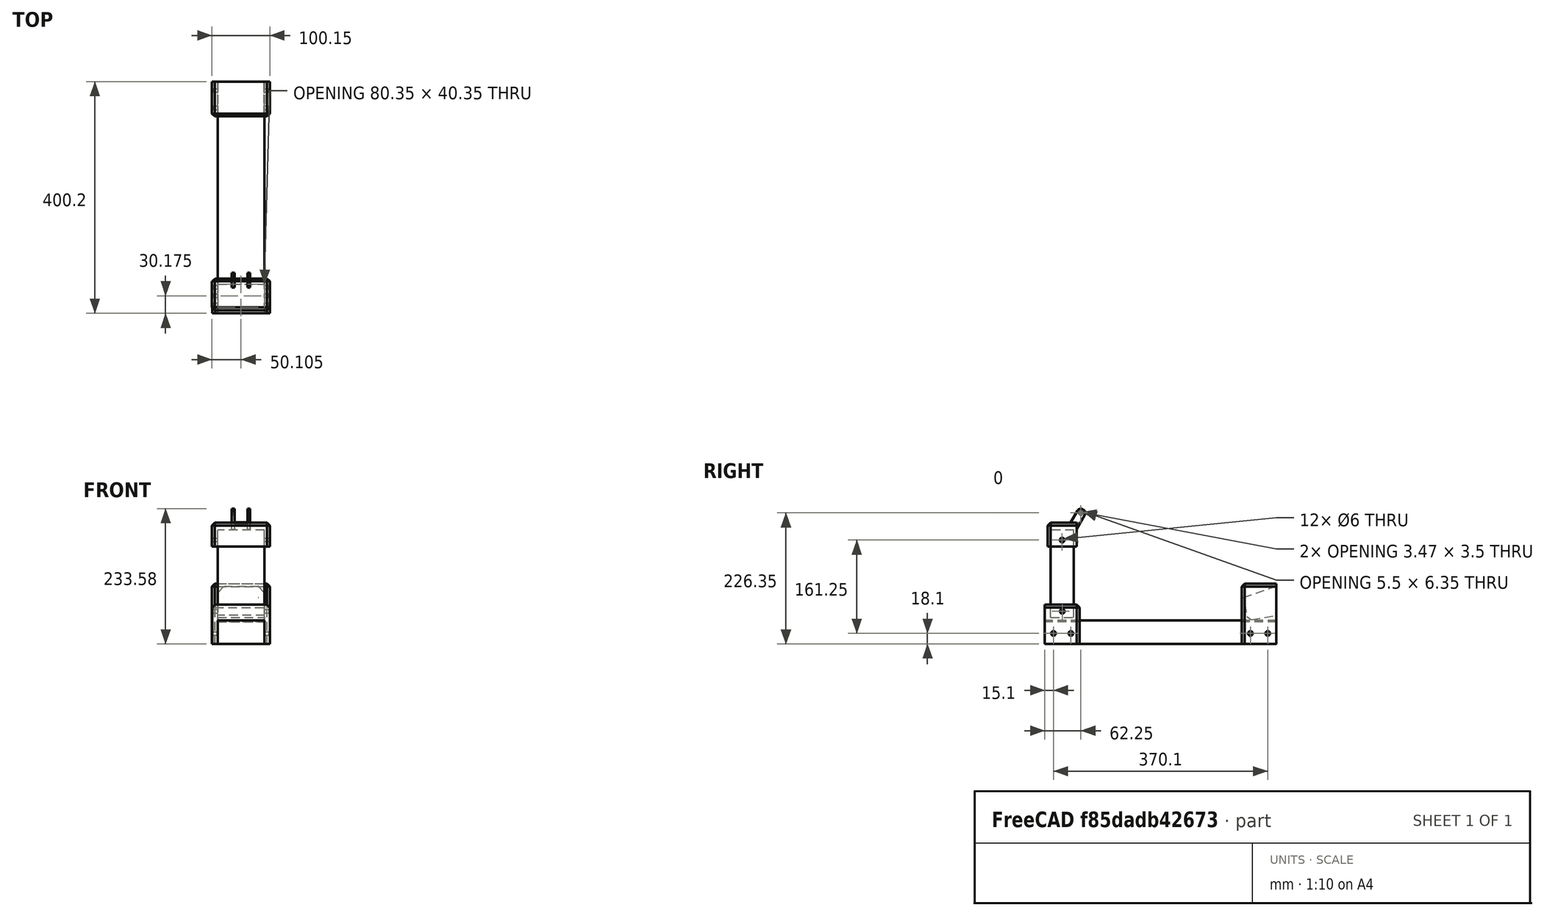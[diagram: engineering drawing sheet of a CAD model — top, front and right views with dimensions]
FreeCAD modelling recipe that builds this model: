
FCSTD DOCUMENT  (FreeCAD 0.19R24276 (Git))
Label: Coil4VapingMaker
License: All rights reserved
LicenseURL: http://en.wikipedia.org/wiki/All_rights_reserved
objects: TechDraw::DrawViewDimension×57, TechDraw::DrawProjGroupItem×9, TechDraw::DrawSVGTemplate×8, TechDraw::DrawViewPart×8, TechDraw::DrawPage×8, Part::Chamfer×6, Part::Box×5, Part::Offset×5, Part::Cut×5, Part::Cylinder×5, Part::Feature×3, TechDraw::DrawProjGroup×3, TechDraw::DrawViewSection×2, Part::MultiFuse×1
note: 30 computed .brp shape members not serialized (recipe doc carries the construction recipe); baked Part::Feature solids carry a one-line shape summary decoded from their .brp

FEATURE [Part::Feature] Part__Feature  label="Chamfer"
  Placement = pos=(-24.075,55,-200.25) rot=(0,0,1;0rad)
  shape: bbox 100 x 60 x 68 mm, 20 faces (baked)
FEATURE [Part::Box] Box001  label="Cube001"
  AttacherType = Attacher::AttachEngine3D
  Height = 151.15
  Length = 80.15
  Width = 40.15
FEATURE [Part::Offset] Offset  label="Offset001"
  Fill = false
  Intersection = false
  Join = 0
  Mode = 0
  Placement = pos=(-24.1,5,-152.9) rot=(0,0,1;0rad)
  SelfIntersection = false
  Source = -> Box001
  Value = 0.1
FEATURE [Part::Cut] Cut
  Base = -> Part__Feature
  Tool = -> Offset
FEATURE [Part::Chamfer] Chamfer  label="Chamfer001"
  Base = -> Cut
  Edges = 5 edges r=5: [Edge3,Edge4,Edge12,Edge19,Edge20]
FEATURE [Part::Cylinder] Cylinder002
  Angle = 360
  AttacherType = Attacher::AttachEngine3D
  Height = 100
  Placement = pos=(-34,25.25,-142) rot=(0,1,0;1.5708rad)
  Radius = 3
FEATURE [Part::Cut] Cut001
  Base = -> Chamfer
  Tool = -> Cylinder002
FEATURE [Part::Chamfer] Chamfer002  label="BaseHolder"
  Base = -> Cut001
  Edges = 2 edges r=1: [Edge5,Edge64]
FEATURE [Part::Box] Box003  label="Cube003"
  AttacherType = Attacher::AttachEngine3D
  Height = 200
  Length = 80.15
  Placement = pos=(0,0,0) rot=(1,0,0;1.5708rad)
  Width = 40.15
FEATURE [Part::Box] Box004  label="Cube004"
  AttacherType = Attacher::AttachEngine3D
  Height = 60
  Length = 100
  Placement = pos=(-9.925,0,2) rot=(1,0,0;1.5708rad)
  Width = 104
FEATURE [Part::Cylinder] Cylinder004
  Angle = 360
  AttacherType = Attacher::AttachEngine3D
  Height = 11
  Placement = pos=(80,-15,20) rot=(0,1,0;1.5708rad)
  Radius = 3
FEATURE [Part::Cylinder] Cylinder005
  Angle = 360
  AttacherType = Attacher::AttachEngine3D
  Height = 11
  Placement = pos=(80,-45,20) rot=(0,1,0;1.5708rad)
  Radius = 3
FEATURE [Part::Cylinder] Cylinder011
  Angle = 360
  AttacherType = Attacher::AttachEngine3D
  Height = 11
  Placement = pos=(-11,-45,20) rot=(0,1,0;1.5708rad)
  Radius = 3
FEATURE [Part::Cylinder] Cylinder012
  Angle = 360
  AttacherType = Attacher::AttachEngine3D
  Height = 11
  Placement = pos=(-11,-15,20) rot=(0,1,0;1.5708rad)
  Radius = 3
FEATURE [Part::Offset] Offset002  label="Offset003"
  Fill = false
  Intersection = false
  Join = 0
  Mode = 0
  SelfIntersection = false
  Source = -> Box003
  Value = 0.1
FEATURE [Part::MultiFuse] Fusion011
  Shapes = -> [Cylinder004,Cylinder005,Cylinder011,Cylinder012]
FEATURE [Part::Feature] Part__Feature002  label="Pad"
  Placement = pos=(0,0,0) rot=(0.57735,0.57735,0.57735;2.0944rad)
  shape: bbox 80.75 x 65 x 50 mm, 6 faces (baked)
FEATURE [Part::Chamfer] Chamfer001  label="Chamfer006"
  Base = -> Part__Feature002
  Edges = 2 edges r=10.65: [Edge11,Edge12]
FEATURE [Part::Chamfer] Chamfer005  label="Chamfer002"
  Base = -> Chamfer001
  Edges = 1 edges r=6.4: [Edge4]
  Placement = pos=(0,-21,68) rot=(1,0,0;0.174533rad)
FEATURE [Part::Offset] Offset003  label="Offset004"
  Fill = false
  Intersection = false
  Join = 0
  Mode = 0
  SelfIntersection = false
  Source = -> Chamfer005
  Value = 0.1
FEATURE [Part::Cut] Cut004
  Base = -> Box004
  Tool = -> Offset002
FEATURE [Part::Cut] Cut005
  Base = -> Cut004
  Tool = -> Fusion011
FEATURE [Part::Cut] Cut006
  Base = -> Cut005
  Tool = -> Offset003
FEATURE [Part::Chamfer] Chamfer006  label="Chamfer007"
  Base = -> Cut006
  Edges = 4 edges r=1: [Edge5,Edge6,Edge45,Edge46]
FEATURE [Part::Chamfer] Chamfer007  label="DrillHolder"
  Base = -> Chamfer006
  Edges = 5 edges r=5: [Edge4,Edge5,Edge12,Edge13,Edge40]
  Placement = pos=(-24.175,395.1,-200.25) rot=(0,0,1;0rad)
FEATURE [Part::Box] Box005  label="Cube005"
  AttacherType = Attacher::AttachEngine3D
  Height = 151.15
  Length = 80.15
  Width = 40.15
FEATURE [Part::Offset] Offset004  label="AluminumProfile_Vert"
  Fill = false
  Intersection = false
  Join = 0
  Mode = 0
  Placement = pos=(-24.1,5,-152.9) rot=(0,0,1;0rad)
  SelfIntersection = false
  Source = -> Box005
  Value = 0.1
FEATURE [Part::Box] Box006  label="Cube006"
  AttacherType = Attacher::AttachEngine3D
  Height = 400
  Length = 80.15
  Placement = pos=(0,0,0) rot=(1,0,0;1.5708rad)
  Width = 40.15
FEATURE [Part::Offset] Offset005  label="AluminumProfile_Hor"
  Fill = false
  Intersection = false
  Join = 0
  Mode = 0
  Placement = pos=(-24.075,395,-198.25) rot=(0,0,1;0rad)
  SelfIntersection = false
  Source = -> Box006
  Value = 0.1
FEATURE [Part::Feature] Part__Feature003  label="ClaptonJig"
  Placement = pos=(31.95,50.15,-6e-15) rot=(0,0,1;3.14159rad)
  shape: bbox 100.2 x 64.92 x 65.08 mm, 286 faces (baked)
FEATURE [TechDraw::DrawSVGTemplate] Template
  EditableTexts = Designed_by_Name=<owner>; Drawing_number=001; FC-Date=12/08/21; FC-SC=1:2; FC-SH=1/8; FC-Title=DrillHolder; Subtitle=Soporte Taladro; Weight=<250gr
  Height = 210
  Orientation = 1
  Width = 297
FEATURE [TechDraw::DrawViewPart] View
  CoarseView = false
  Direction = (0.577,-0.577,0.577)
  Focus = 100
  HardHidden = false
  IsoCount = 0
  IsoHidden = false
  IsoVisible = false
  LockPosition = false
  Perspective = false
  Rotation = 0
  Scale = 0.5
  ScaleType = 0
  SeamHidden = false
  SeamVisible = true
  SmoothHidden = false
  SmoothVisible = true
  Source = -> [Chamfer007]
  X = 213.955
  XDirection = (0.707,0.707,0)
  Y = 142.792
FEATURE [TechDraw::DrawProjGroupItem] ProjItem  label="Front"
  CoarseView = false
  Direction = (0,-1,0)
  Focus = 100
  HardHidden = false
  IsoCount = 0
  IsoHidden = false
  IsoVisible = false
  LockPosition = true
  Perspective = false
  Rotation = 0
  RotationVector = (1,0,0)
  ScaleType = 2
  SeamHidden = false
  SeamVisible = true
  SmoothHidden = false
  SmoothVisible = true
  Source = -> [Chamfer007]
  Type = 0
  X = 0
  XDirection = (1,0,0)
  Y = 0
FEATURE [TechDraw::DrawProjGroupItem] ProjItem001  label="Right"
  CoarseView = false
  Direction = (1,-1e-16,0)
  Focus = 100
  HardHidden = false
  IsoCount = 0
  IsoHidden = false
  IsoVisible = false
  LockPosition = false
  Perspective = false
  Rotation = 0
  RotationVector = (1,0,0)
  ScaleType = 2
  SeamHidden = false
  SeamVisible = true
  SmoothHidden = false
  SmoothVisible = true
  Source = -> [Chamfer007]
  Type = 2
  X = -54.9943
  XDirection = (1e-16,1,0)
  Y = 0
FEATURE [TechDraw::DrawProjGroupItem] ProjItem002  label="Top"
  CoarseView = false
  Direction = (0,0,1)
  Focus = 100
  HardHidden = false
  IsoCount = 0
  IsoHidden = false
  IsoVisible = false
  LockPosition = false
  Perspective = false
  Rotation = 0
  RotationVector = (1,0,0)
  ScaleType = 2
  SeamHidden = false
  SeamVisible = true
  SmoothHidden = false
  SmoothVisible = true
  Source = -> [Chamfer007]
  Type = 4
  X = 0
  XDirection = (1,0,0)
  Y = -77.9943
FEATURE [TechDraw::DrawProjGroup] ProjGroup
  Anchor = -> ProjItem
  AutoDistribute = true
  LockPosition = false
  ProjectionType = 0
  Rotation = 0
  Scale = 0.5
  ScaleType = 0
  Source = -> [Chamfer007]
  Views = -> [ProjItem,ProjItem001,ProjItem002]
  X = 113.619
  Y = 153.955
  spacingX = 15
  spacingY = 15
FEATURE [TechDraw::DrawViewDimension] Dimension
  Arbitrary = false
  ArbitraryTolerances = false
  EqualTolerance = true
  FormatSpec = %.2f
  FormatSpecOverTolerance = %+.2f
  FormatSpecUnderTolerance = %+.2f
  Inverted = false
  LockPosition = false
  MeasureType = 1
  OverTolerance = 0
  References2D = -> [ProjItem001]
  Rotation = 0
  Scale = 0.5
  ScaleType = 0
  TheoreticalExact = false
  Type = 1
  UnderTolerance = 0
  X = -4.62931
  Y = -45.9172
FEATURE [TechDraw::DrawViewDimension] Dimension001
  Arbitrary = false
  ArbitraryTolerances = false
  EqualTolerance = true
  FormatSpec = %.2f
  FormatSpecOverTolerance = %+.2f
  FormatSpecUnderTolerance = %+.2f
  Inverted = false
  LockPosition = false
  MeasureType = 1
  OverTolerance = 0
  References2D = -> [ProjItem001]
  Rotation = 0
  Scale = 0.5
  ScaleType = 0
  TheoreticalExact = false
  Type = 2
  UnderTolerance = 0
  X = -32.0672
  Y = 3.55664
FEATURE [TechDraw::DrawViewDimension] Dimension002
  Arbitrary = false
  ArbitraryTolerances = false
  EqualTolerance = true
  FormatSpec = %.2f
  FormatSpecOverTolerance = %+.2f
  FormatSpecUnderTolerance = %+.2f
  Inverted = false
  LockPosition = false
  MeasureType = 1
  OverTolerance = 0
  References2D = -> [ProjItem002]
  Rotation = 0
  Scale = 0.5
  ScaleType = 0
  TheoreticalExact = false
  Type = 1
  UnderTolerance = 0
  X = -5.33496
  Y = 31.7105
FEATURE [TechDraw::DrawViewDimension] Dimension003
  Arbitrary = false
  ArbitraryTolerances = false
  EqualTolerance = true
  FormatSpec = ⌀%.2f
  FormatSpecOverTolerance = %+.2f
  FormatSpecUnderTolerance = %+.2f
  Inverted = false
  LockPosition = false
  MeasureType = 1
  OverTolerance = 0
  References2D = -> [ProjItem001]
  Rotation = 0
  Scale = 0.5
  ScaleType = 0
  TheoreticalExact = false
  Type = 5
  UnderTolerance = 0
  X = -3.34743
  Y = -7.14989
FEATURE [TechDraw::DrawViewDimension] Dimension004
  Arbitrary = false
  ArbitraryTolerances = false
  EqualTolerance = true
  FormatSpec = %.2f
  FormatSpecOverTolerance = %+.2f
  FormatSpecUnderTolerance = %+.2f
  Inverted = false
  LockPosition = false
  MeasureType = 1
  OverTolerance = 0
  References2D = -> [ProjItem]
  Rotation = 0
  Scale = 0.5
  ScaleType = 0
  TheoreticalExact = false
  Type = 1
  UnderTolerance = 0
  X = -4.14507
  Y = 5.79607
FEATURE [TechDraw::DrawPage] Page  label="DrillHolder_Vistas"
  KeepUpdated = true
  NextBalloonIndex = 1
  ProjectionType = 0
  Scale = 0.5
  Template = -> Template
  Views = -> [View,ProjGroup,Dimension,Dimension001,Dimension002,Dimension003,Dimension004]
FEATURE [TechDraw::DrawSVGTemplate] Template001
  EditableTexts = Designed_by_Name=Designed by Name; Drawing_number=001; FC-Date=12/8/21; FC-SC=1:1; FC-SH=4/8; FC-Title=BaseHolder; Subtitle=Pieza Base; Weight=<250gr
  Height = 210
  Orientation = 1
  Width = 297
FEATURE [TechDraw::DrawViewPart] View001
  CoarseView = false
  Direction = (0.577,-0.577,0.577)
  Focus = 100
  HardHidden = false
  IsoCount = 0
  IsoHidden = false
  IsoVisible = false
  LockPosition = false
  Perspective = false
  Rotation = 0
  ScaleType = 0
  SeamHidden = false
  SeamVisible = true
  SmoothHidden = false
  SmoothVisible = true
  Source = -> [Chamfer002]
  X = 210.838
  XDirection = (0.707,0.707,0)
  Y = 130.325
FEATURE [TechDraw::DrawProjGroupItem] ProjItem003  label="Front001"
  CoarseView = false
  Direction = (0,-1,0)
  Focus = 100
  HardHidden = false
  IsoCount = 0
  IsoHidden = false
  IsoVisible = false
  LockPosition = true
  Perspective = false
  Rotation = 0
  RotationVector = (1,0,0)
  Scale = 0.5
  ScaleType = 2
  SeamHidden = false
  SeamVisible = true
  SmoothHidden = false
  SmoothVisible = true
  Source = -> [Chamfer002]
  Type = 0
  X = 0
  XDirection = (1,0,0)
  Y = 0
FEATURE [TechDraw::DrawProjGroupItem] ProjItem004  label="Right001"
  CoarseView = false
  Direction = (1,-1e-16,0)
  Focus = 100
  HardHidden = false
  IsoCount = 0
  IsoHidden = false
  IsoVisible = false
  LockPosition = false
  Perspective = false
  Rotation = 0
  RotationVector = (1,0,0)
  ScaleType = 2
  SeamHidden = false
  SeamVisible = true
  SmoothHidden = false
  SmoothVisible = true
  Source = -> [Chamfer002]
  Type = 2
  X = -55
  XDirection = (1e-16,1,0)
  Y = 0
FEATURE [TechDraw::DrawProjGroupItem] ProjItem005  label="Top001"
  CoarseView = false
  Direction = (0,0,1)
  Focus = 100
  HardHidden = false
  IsoCount = 0
  IsoHidden = false
  IsoVisible = false
  LockPosition = false
  Perspective = false
  Rotation = 0
  RotationVector = (1,0,0)
  ScaleType = 2
  SeamHidden = false
  SeamVisible = true
  SmoothHidden = false
  SmoothVisible = true
  Source = -> [Chamfer002]
  Type = 4
  X = 0
  XDirection = (1,0,0)
  Y = -51
FEATURE [TechDraw::DrawProjGroup] ProjGroup001
  Anchor = -> ProjItem003
  AutoDistribute = true
  LockPosition = false
  ProjectionType = 0
  Rotation = 0
  Scale = 0.5
  ScaleType = 2
  Source = -> [Chamfer002]
  Views = -> [ProjItem003,ProjItem004,ProjItem005]
  X = 99.7987
  Y = 171.234
  spacingX = 15
  spacingY = 15
FEATURE [TechDraw::DrawViewDimension] Dimension005
  Arbitrary = false
  ArbitraryTolerances = false
  EqualTolerance = true
  FormatSpec = %.2f
  FormatSpecOverTolerance = %+.2f
  FormatSpecUnderTolerance = %+.2f
  Inverted = false
  LockPosition = false
  MeasureType = 1
  OverTolerance = 0
  References2D = -> [ProjItem005]
  Rotation = 0
  ScaleType = 0
  TheoreticalExact = false
  Type = 1
  UnderTolerance = 0
  X = -2.25469
  Y = -26.7244
FEATURE [TechDraw::DrawViewDimension] Dimension006
  Arbitrary = false
  ArbitraryTolerances = false
  EqualTolerance = true
  FormatSpec = %.2f
  FormatSpecOverTolerance = %+.2f
  FormatSpecUnderTolerance = %+.2f
  Inverted = false
  LockPosition = false
  MeasureType = 1
  OverTolerance = 0
  References2D = -> [ProjItem005]
  Rotation = 0
  ScaleType = 0
  TheoreticalExact = false
  Type = 2
  UnderTolerance = 0
  X = -39.3074
  Y = 2.48016
FEATURE [TechDraw::DrawViewDimension] Dimension007
  Arbitrary = false
  ArbitraryTolerances = false
  EqualTolerance = true
  FormatSpec = %.2f
  FormatSpecOverTolerance = %+.2f
  FormatSpecUnderTolerance = %+.2f
  Inverted = false
  LockPosition = false
  MeasureType = 1
  OverTolerance = 0
  References2D = -> [ProjItem003]
  Rotation = 0
  ScaleType = 0
  TheoreticalExact = false
  Type = 1
  UnderTolerance = 0
  X = -3.13151
  Y = 11.6261
FEATURE [TechDraw::DrawViewDimension] Dimension008
  Arbitrary = false
  ArbitraryTolerances = false
  EqualTolerance = true
  FormatSpec = ⌀%.2f
  FormatSpecOverTolerance = %+.2f
  FormatSpecUnderTolerance = %+.2f
  Inverted = false
  LockPosition = false
  MeasureType = 1
  OverTolerance = 0
  References2D = -> [ProjItem004]
  Rotation = 0
  ScaleType = 0
  TheoreticalExact = false
  Type = 5
  UnderTolerance = 0
  X = -4.5407
  Y = 3.91439
FEATURE [TechDraw::DrawViewDimension] Dimension009
  Arbitrary = false
  ArbitraryTolerances = false
  EqualTolerance = true
  FormatSpec = %.2f
  FormatSpecOverTolerance = %+.2f
  FormatSpecUnderTolerance = %+.2f
  Inverted = false
  LockPosition = false
  MeasureType = 1
  OverTolerance = 0
  References2D = -> [ProjItem004]
  Rotation = 0
  ScaleType = 0
  TheoreticalExact = false
  Type = 2
  UnderTolerance = 0
  X = -26.6
  Y = 4
FEATURE [TechDraw::DrawPage] Page001  label="BaseHolder_Vistas"
  KeepUpdated = true
  NextBalloonIndex = 1
  ProjectionType = 0
  Template = -> Template001
  Views = -> [View001,ProjGroup001,Dimension005,Dimension006,Dimension007,Dimension008,Dimension009]
FEATURE [TechDraw::DrawSVGTemplate] Template002
  EditableTexts = Designed_by_Name=<owner>; Drawing_number=001; FC-Date=12/8/21; FC-SC=1:1; FC-SH=6/8; FC-Title=ClaptonJig; Subtitle=Soporte Quitavueltas; Weight=<250gr
  Height = 210
  Orientation = 1
  Width = 297
FEATURE [TechDraw::DrawViewPart] View002
  CoarseView = false
  Direction = (0.577,-0.577,0.577)
  Focus = 100
  HardHidden = false
  IsoCount = 0
  IsoHidden = false
  IsoVisible = false
  LockPosition = false
  Perspective = false
  Rotation = 0
  ScaleType = 0
  SeamHidden = false
  SeamVisible = true
  SmoothHidden = false
  SmoothVisible = true
  Source = -> [Part__Feature003]
  X = 212.006
  XDirection = (0.707,0.707,0)
  Y = 134.221
FEATURE [TechDraw::DrawProjGroupItem] ProjItem006  label="Front002"
  CoarseView = false
  Direction = (0,-1,0)
  Focus = 100
  HardHidden = false
  IsoCount = 0
  IsoHidden = false
  IsoVisible = false
  LockPosition = true
  Perspective = false
  Rotation = 0
  RotationVector = (1,0,0)
  Scale = 0.5
  ScaleType = 2
  SeamHidden = false
  SeamVisible = true
  SmoothHidden = false
  SmoothVisible = true
  Source = -> [Part__Feature003]
  Type = 0
  X = 0
  XDirection = (1,0,0)
  Y = 0
FEATURE [TechDraw::DrawProjGroupItem] ProjItem007  label="Right002"
  CoarseView = false
  Direction = (1,-1e-16,0)
  Focus = 100
  HardHidden = false
  IsoCount = 0
  IsoHidden = false
  IsoVisible = false
  LockPosition = false
  Perspective = false
  Rotation = 0
  RotationVector = (1,0,0)
  ScaleType = 2
  SeamHidden = false
  SeamVisible = true
  SmoothHidden = false
  SmoothVisible = true
  Source = -> [Part__Feature003]
  Type = 2
  X = -56.2671
  XDirection = (1e-16,1,0)
  Y = 0
FEATURE [TechDraw::DrawProjGroupItem] ProjItem008  label="Top002"
  CoarseView = false
  Direction = (0,0,1)
  Focus = 100
  HardHidden = false
  IsoCount = 0
  IsoHidden = false
  IsoVisible = false
  LockPosition = false
  Perspective = false
  Rotation = 0
  RotationVector = (1,0,0)
  ScaleType = 2
  SeamHidden = false
  SeamVisible = true
  SmoothHidden = false
  SmoothVisible = true
  Source = -> [Part__Feature003]
  Type = 4
  X = 0
  XDirection = (1,0,0)
  Y = -47.5798
FEATURE [TechDraw::DrawProjGroup] ProjGroup002
  Anchor = -> ProjItem006
  AutoDistribute = true
  LockPosition = false
  ProjectionType = 0
  Rotation = 0
  Scale = 0.5
  ScaleType = 2
  Source = -> [Part__Feature003]
  Views = -> [ProjItem006,ProjItem007,ProjItem008]
  X = 108.37
  Y = 169.286
  spacingX = 15
  spacingY = 15
FEATURE [TechDraw::DrawViewDimension] Dimension010
  Arbitrary = false
  ArbitraryTolerances = false
  EqualTolerance = true
  FormatSpec = %.2f
  FormatSpecOverTolerance = %+.2f
  FormatSpecUnderTolerance = %+.2f
  Inverted = false
  LockPosition = false
  MeasureType = 1
  OverTolerance = 0
  References2D = -> [ProjItem008]
  Rotation = 0
  ScaleType = 0
  TheoreticalExact = false
  Type = 2
  UnderTolerance = 0
  X = -42.276
  Y = -0.347528
FEATURE [TechDraw::DrawViewDimension] Dimension011
  Arbitrary = false
  ArbitraryTolerances = false
  EqualTolerance = true
  FormatSpec = %.2f
  FormatSpecOverTolerance = %+.2f
  FormatSpecUnderTolerance = %+.2f
  Inverted = false
  LockPosition = false
  MeasureType = 1
  OverTolerance = 0
  References2D = -> [ProjItem008]
  Rotation = 0
  ScaleType = 0
  TheoreticalExact = false
  Type = 1
  UnderTolerance = 0
  X = -3.38204
  Y = -27.7086
FEATURE [TechDraw::DrawViewDimension] Dimension012
  Arbitrary = false
  ArbitraryTolerances = false
  EqualTolerance = true
  FormatSpec = %.2f
  FormatSpecOverTolerance = %+.2f
  FormatSpecUnderTolerance = %+.2f
  Inverted = false
  LockPosition = false
  MeasureType = 1
  OverTolerance = 0
  References2D = -> [ProjItem007]
  Rotation = 0
  ScaleType = 0
  TheoreticalExact = false
  Type = 2
  UnderTolerance = 0
  X = -33.919
  Y = -3.12619
FEATURE [TechDraw::DrawViewDimension] Dimension013
  Arbitrary = false
  ArbitraryTolerances = false
  EqualTolerance = true
  FormatSpec = ⌀%.2f
  FormatSpecOverTolerance = %+.2f
  FormatSpecUnderTolerance = %+.2f
  Inverted = false
  LockPosition = false
  MeasureType = 1
  OverTolerance = 0
  References2D = -> [ProjItem007]
  Rotation = 0
  ScaleType = 0
  TheoreticalExact = false
  Type = 5
  UnderTolerance = 0
  X = -6.57618
  Y = -4.32149
FEATURE [TechDraw::DrawPage] Page002  label="ClaptonJig_Vistas"
  KeepUpdated = true
  NextBalloonIndex = 1
  ProjectionType = 0
  Template = -> Template002
  Views = -> [View002,ProjGroup002,Dimension010,Dimension011,Dimension012,Dimension013]
FEATURE [TechDraw::DrawSVGTemplate] Template003
  EditableTexts = Designed_by_Name=<owner>; Drawing_number=001; FC-Date=15/8/21; FC-SC=1:1; FC-SH=7/8; FC-Title=ClaptonJig; Subtitle=Soporte Quitavueltas; Weight=<250gr
  Height = 210
  Orientation = 1
  Width = 297
FEATURE [TechDraw::DrawViewPart] View003
  CoarseView = false
  Direction = (0.577,-0.577,0.577)
  Focus = 100
  HardHidden = false
  IsoCount = 0
  IsoHidden = false
  IsoVisible = false
  LockPosition = false
  Perspective = false
  Rotation = 0
  ScaleType = 0
  SeamHidden = false
  SeamVisible = true
  SmoothHidden = false
  SmoothVisible = true
  Source = -> [Part__Feature003]
  X = 140.708
  XDirection = (0.707,0.707,0)
  Y = 129.935
FEATURE [TechDraw::DrawViewDimension] Dimension014
  Arbitrary = false
  ArbitraryTolerances = false
  EqualTolerance = true
  FormatSpec = %.2f
  FormatSpecOverTolerance = %+.2f
  FormatSpecUnderTolerance = %+.2f
  Inverted = false
  LockPosition = false
  MeasureType = 1
  OverTolerance = 0
  References2D = -> [View003]
  Rotation = 0
  ScaleType = 0
  TheoreticalExact = false
  Type = 0
  UnderTolerance = 0
  X = -96.3038
  Y = 22.7886
FEATURE [TechDraw::DrawViewDimension] Dimension015
  Arbitrary = false
  ArbitraryTolerances = false
  EqualTolerance = true
  FormatSpec = %.2f
  FormatSpecOverTolerance = %+.2f
  FormatSpecUnderTolerance = %+.2f
  Inverted = false
  LockPosition = false
  MeasureType = 1
  OverTolerance = 0
  References2D = -> [View003]
  Rotation = 0
  ScaleType = 0
  TheoreticalExact = false
  Type = 1
  UnderTolerance = 0
  X = 28.0409
  Y = -62.7119
FEATURE [TechDraw::DrawViewDimension] Dimension016
  Arbitrary = false
  ArbitraryTolerances = false
  EqualTolerance = true
  FormatSpec = %.2f
  FormatSpecOverTolerance = %+.2f
  FormatSpecUnderTolerance = %+.2f
  Inverted = false
  LockPosition = false
  MeasureType = 1
  OverTolerance = 0
  References2D = -> [View003]
  Rotation = 0
  ScaleType = 0
  TheoreticalExact = false
  Type = 0
  UnderTolerance = 0
  X = 59.9311
  Y = -21.7139
FEATURE [TechDraw::DrawViewDimension] Dimension017
  Arbitrary = false
  ArbitraryTolerances = false
  EqualTolerance = true
  FormatSpec = %.2f
  FormatSpecOverTolerance = %+.2f
  FormatSpecUnderTolerance = %+.2f
  Inverted = false
  LockPosition = false
  MeasureType = 1
  OverTolerance = 0
  References2D = -> [View003]
  Rotation = 0
  ScaleType = 0
  TheoreticalExact = false
  Type = 0
  UnderTolerance = 0
  X = 36.7201
  Y = 49.4149
FEATURE [TechDraw::DrawViewDimension] Dimension018
  Arbitrary = false
  ArbitraryTolerances = false
  EqualTolerance = true
  FormatSpec = %.2f
  FormatSpecOverTolerance = %+.2f
  FormatSpecUnderTolerance = %+.2f
  Inverted = false
  LockPosition = false
  MeasureType = 1
  OverTolerance = 0
  References2D = -> [View003]
  Rotation = 0
  ScaleType = 0
  TheoreticalExact = false
  Type = 0
  UnderTolerance = 0
  X = -8.95626
  Y = 48.4178
FEATURE [TechDraw::DrawViewDimension] Dimension019
  Arbitrary = false
  ArbitraryTolerances = false
  EqualTolerance = true
  FormatSpec = %.2f
  FormatSpecOverTolerance = %+.2f
  FormatSpecUnderTolerance = %+.2f
  Inverted = false
  LockPosition = false
  MeasureType = 1
  OverTolerance = 0
  References2D = -> [View003]
  Rotation = 0
  ScaleType = 0
  TheoreticalExact = false
  Type = 0
  UnderTolerance = 0
  X = -1.94468
  Y = 15.1715
FEATURE [TechDraw::DrawViewDimension] Dimension020
  Arbitrary = false
  ArbitraryTolerances = false
  EqualTolerance = true
  FormatSpec = %.2f
  FormatSpecOverTolerance = %+.2f
  FormatSpecUnderTolerance = %+.2f
  Inverted = false
  LockPosition = false
  MeasureType = 1
  OverTolerance = 0
  References2D = -> [View003]
  Rotation = 0
  ScaleType = 0
  TheoreticalExact = false
  Type = 0
  UnderTolerance = 0
  X = 49.5183
  Y = 23.744
FEATURE [TechDraw::DrawViewDimension] Dimension021
  Arbitrary = false
  ArbitraryTolerances = false
  EqualTolerance = true
  FormatSpec = %.2f
  FormatSpecOverTolerance = %+.2f
  FormatSpecUnderTolerance = %+.2f
  Inverted = false
  LockPosition = false
  MeasureType = 1
  OverTolerance = 0
  References2D = -> [View003]
  Rotation = 0
  ScaleType = 0
  TheoreticalExact = false
  Type = 0
  UnderTolerance = 0
  X = 75.9646
  Y = -9.82824
FEATURE [TechDraw::DrawPage] Page003  label="ClaptonJig_Cotas"
  KeepUpdated = true
  NextBalloonIndex = 1
  ProjectionType = 0
  Template = -> Template003
  Views = -> [View003,Dimension014,Dimension015,Dimension016,Dimension017,Dimension018,Dimension019,Dimension020,Dimension021]
FEATURE [TechDraw::DrawSVGTemplate] Template004
  EditableTexts = Designed_by_Name=<owner>; Drawing_number=001; FC-Date=15/8/21; FC-SC=1:1; FC-SH=2/8; FC-Title=DrillHolder; Subtitle=Soporte Taladro; Weight=<250gr
  Height = 210
  Orientation = 1
  Width = 297
FEATURE [TechDraw::DrawViewPart] View004
  CoarseView = false
  Direction = (0.577,-0.577,0.577)
  Focus = 100
  HardHidden = false
  IsoCount = 0
  IsoHidden = false
  IsoVisible = false
  LockPosition = false
  Perspective = false
  Rotation = 0
  ScaleType = 0
  SeamHidden = false
  SeamVisible = true
  SmoothHidden = false
  SmoothVisible = true
  Source = -> [Chamfer007]
  X = 111.487
  XDirection = (0.707,0.707,0)
  Y = 124.481
FEATURE [TechDraw::DrawViewDimension] Dimension022
  Arbitrary = false
  ArbitraryTolerances = false
  EqualTolerance = true
  FormatSpec = %.2f
  FormatSpecOverTolerance = %+.2f
  FormatSpecUnderTolerance = %+.2f
  Inverted = false
  LockPosition = false
  MeasureType = 1
  OverTolerance = 0
  References2D = -> [View004]
  Rotation = 0
  ScaleType = 0
  TheoreticalExact = false
  Type = 0
  UnderTolerance = 0
  X = 69.033
  Y = 25.2722
FEATURE [TechDraw::DrawViewDimension] Dimension023
  Arbitrary = false
  ArbitraryTolerances = false
  EqualTolerance = true
  FormatSpec = %.2f
  FormatSpecOverTolerance = %+.2f
  FormatSpecUnderTolerance = %+.2f
  Inverted = false
  LockPosition = false
  MeasureType = 1
  OverTolerance = 0
  References2D = -> [View004]
  Rotation = 0
  ScaleType = 0
  TheoreticalExact = false
  Type = 0
  UnderTolerance = 0
  X = -13.787
  Y = -61.7372
FEATURE [TechDraw::DrawViewDimension] Dimension024
  Arbitrary = false
  ArbitraryTolerances = false
  EqualTolerance = true
  FormatSpec = %.2f
  FormatSpecOverTolerance = %+.2f
  FormatSpecUnderTolerance = %+.2f
  Inverted = false
  LockPosition = false
  MeasureType = 1
  OverTolerance = 0
  References2D = -> [View004]
  Rotation = 0
  ScaleType = 0
  TheoreticalExact = false
  Type = 0
  UnderTolerance = 0
  X = 65.1832
  Y = -34.3489
FEATURE [TechDraw::DrawViewDimension] Dimension025
  Arbitrary = false
  ArbitraryTolerances = false
  EqualTolerance = true
  FormatSpec = ⌀%.2f
  FormatSpecOverTolerance = %+.2f
  FormatSpecUnderTolerance = %+.2f
  Inverted = false
  LockPosition = false
  MeasureType = 1
  OverTolerance = 0
  References2D = -> [View004]
  Rotation = 0
  ScaleType = 0
  TheoreticalExact = false
  Type = 5
  UnderTolerance = 0
  X = -27.1086
  Y = 1.72849
FEATURE [TechDraw::DrawViewDimension] Dimension026
  Arbitrary = false
  ArbitraryTolerances = false
  EqualTolerance = true
  FormatSpec = %.2f
  FormatSpecOverTolerance = %+.2f
  FormatSpecUnderTolerance = %+.2f
  Inverted = false
  LockPosition = false
  MeasureType = 1
  OverTolerance = 0
  References2D = -> [View004]
  Rotation = 0
  ScaleType = 0
  TheoreticalExact = false
  Type = 0
  UnderTolerance = 0
  X = -81.033
  Y = 41.5609
FEATURE [TechDraw::DrawViewDimension] Dimension027
  Arbitrary = false
  ArbitraryTolerances = false
  EqualTolerance = true
  FormatSpec = %.2f
  FormatSpecOverTolerance = %+.2f
  FormatSpecUnderTolerance = %+.2f
  Inverted = false
  LockPosition = false
  MeasureType = 1
  OverTolerance = 0
  References2D = -> [View004]
  Rotation = 0
  ScaleType = 0
  TheoreticalExact = false
  Type = 2
  UnderTolerance = 0
  X = -78.2153
  Y = -20.5932
FEATURE [TechDraw::DrawViewDimension] Dimension028
  Arbitrary = false
  ArbitraryTolerances = false
  EqualTolerance = true
  FormatSpec = %.2f
  FormatSpecOverTolerance = %+.2f
  FormatSpecUnderTolerance = %+.2f
  Inverted = false
  LockPosition = false
  MeasureType = 1
  OverTolerance = 0
  References2D = -> [View004]
  Rotation = 0
  ScaleType = 0
  TheoreticalExact = false
  Type = 2
  UnderTolerance = 0
  X = -7.66706
  Y = -12.1003
FEATURE [TechDraw::DrawPage] Page004  label="DrillHolder_Cotas"
  KeepUpdated = true
  NextBalloonIndex = 1
  ProjectionType = 0
  Template = -> Template004
  Views = -> [View004,Dimension022,Dimension023,Dimension024,Dimension025,Dimension026,Dimension027,Dimension028]
FEATURE [TechDraw::DrawSVGTemplate] Template005
  EditableTexts = Designed_by_Name=<owner>; Drawing_number=001; FC-Date=15/8/21; FC-SC=1:1; FC-SH=5/8; FC-Title=BaseHolder; Subtitle=Pieza Base; Weight=250gr
  Height = 210
  Orientation = 1
  Width = 297
FEATURE [TechDraw::DrawViewPart] View005
  CoarseView = false
  Direction = (0.577,-0.577,0.577)
  Focus = 100
  HardHidden = false
  IsoCount = 0
  IsoHidden = false
  IsoVisible = false
  LockPosition = false
  Perspective = false
  Rotation = 0
  ScaleType = 0
  SeamHidden = false
  SeamVisible = true
  SmoothHidden = false
  SmoothVisible = true
  Source = -> [Chamfer002]
  X = 136.5
  XDirection = (0.707,0.707,0)
  Y = 131
FEATURE [TechDraw::DrawViewDimension] Dimension029
  Arbitrary = false
  ArbitraryTolerances = false
  EqualTolerance = true
  FormatSpec = %.2f
  FormatSpecOverTolerance = %+.2f
  FormatSpecUnderTolerance = %+.2f
  Inverted = false
  LockPosition = false
  MeasureType = 1
  OverTolerance = 0
  References2D = -> [View005]
  Rotation = 0
  ScaleType = 0
  TheoreticalExact = false
  Type = 0
  UnderTolerance = 0
  X = -84.5271
  Y = -15.1602
FEATURE [TechDraw::DrawViewDimension] Dimension030
  Arbitrary = false
  ArbitraryTolerances = false
  EqualTolerance = true
  FormatSpec = %.2f
  FormatSpecOverTolerance = %+.2f
  FormatSpecUnderTolerance = %+.2f
  Inverted = false
  LockPosition = false
  MeasureType = 1
  OverTolerance = 0
  References2D = -> [View005]
  Rotation = 0
  ScaleType = 0
  TheoreticalExact = false
  Type = 0
  UnderTolerance = 0
  X = -27.5638
  Y = -60.374
FEATURE [TechDraw::DrawViewDimension] Dimension031
  Arbitrary = false
  ArbitraryTolerances = false
  EqualTolerance = true
  FormatSpec = %.2f
  FormatSpecOverTolerance = %+.2f
  FormatSpecUnderTolerance = %+.2f
  Inverted = false
  LockPosition = false
  MeasureType = 1
  OverTolerance = 0
  References2D = -> [View005]
  Rotation = 0
  ScaleType = 0
  TheoreticalExact = false
  Type = 2
  UnderTolerance = 0
  X = -6.63742
  Y = -33.9938
FEATURE [TechDraw::DrawViewDimension] Dimension032
  Arbitrary = false
  ArbitraryTolerances = false
  EqualTolerance = true
  FormatSpec = %.2f
  FormatSpecOverTolerance = %+.2f
  FormatSpecUnderTolerance = %+.2f
  Inverted = false
  LockPosition = false
  MeasureType = 1
  OverTolerance = 0
  References2D = -> [View005]
  Rotation = 0
  ScaleType = 0
  TheoreticalExact = false
  Type = 2
  UnderTolerance = 0
  X = -19.5638
  Y = -29.8543
FEATURE [TechDraw::DrawViewDimension] Dimension033
  Arbitrary = false
  ArbitraryTolerances = false
  EqualTolerance = true
  FormatSpec = %.2f
  FormatSpecOverTolerance = %+.2f
  FormatSpecUnderTolerance = %+.2f
  Inverted = false
  LockPosition = false
  MeasureType = 1
  OverTolerance = 0
  References2D = -> [View005]
  Rotation = 0
  ScaleType = 0
  TheoreticalExact = false
  Type = 0
  UnderTolerance = 0
  X = 81.033
  Y = 20.1753
FEATURE [TechDraw::DrawViewDimension] Dimension034
  Arbitrary = false
  ArbitraryTolerances = false
  EqualTolerance = true
  FormatSpec = %.2f
  FormatSpecOverTolerance = %+.2f
  FormatSpecUnderTolerance = %+.2f
  Inverted = false
  LockPosition = false
  MeasureType = 1
  OverTolerance = 0
  References2D = -> [View005]
  Rotation = 0
  ScaleType = 0
  TheoreticalExact = false
  Type = 0
  UnderTolerance = 0
  X = 2.40795
  Y = 52.2698
FEATURE [TechDraw::DrawViewDimension] Dimension035
  Arbitrary = false
  ArbitraryTolerances = false
  EqualTolerance = true
  FormatSpec = ⌀%.2f
  FormatSpecOverTolerance = %+.2f
  FormatSpecUnderTolerance = %+.2f
  Inverted = false
  LockPosition = false
  MeasureType = 1
  OverTolerance = 0
  References2D = -> [View005]
  Rotation = 0
  ScaleType = 0
  TheoreticalExact = false
  Type = 5
  UnderTolerance = 0
  X = -58.8802
  Y = 41.3328
FEATURE [TechDraw::DrawViewDimension] Dimension036
  Arbitrary = false
  ArbitraryTolerances = false
  EqualTolerance = true
  FormatSpec = %.2f
  FormatSpecOverTolerance = %+.2f
  FormatSpecUnderTolerance = %+.2f
  Inverted = false
  LockPosition = false
  MeasureType = 1
  OverTolerance = 0
  References2D = -> [View005]
  Rotation = 0
  ScaleType = 0
  TheoreticalExact = false
  Type = 0
  UnderTolerance = 0
  X = 74.3479
  Y = -2.25968
FEATURE [TechDraw::DrawViewDimension] Dimension037
  Arbitrary = false
  ArbitraryTolerances = false
  EqualTolerance = true
  FormatSpec = %.2f
  FormatSpecOverTolerance = %+.2f
  FormatSpecUnderTolerance = %+.2f
  Inverted = false
  LockPosition = false
  MeasureType = 1
  OverTolerance = 0
  References2D = -> [View005]
  Rotation = 0
  ScaleType = 0
  TheoreticalExact = false
  Type = 0
  UnderTolerance = 0
  X = -24.3101
  Y = 15.0136
FEATURE [TechDraw::DrawViewDimension] Dimension038
  Arbitrary = false
  ArbitraryTolerances = false
  EqualTolerance = true
  FormatSpec = %.2f
  FormatSpecOverTolerance = %+.2f
  FormatSpecUnderTolerance = %+.2f
  Inverted = false
  LockPosition = false
  MeasureType = 1
  OverTolerance = 0
  References2D = -> [View005]
  Rotation = 0
  ScaleType = 0
  TheoreticalExact = false
  Type = 0
  UnderTolerance = 0
  X = 46.7521
  Y = -3.72018
FEATURE [TechDraw::DrawViewDimension] Dimension039
  Arbitrary = false
  ArbitraryTolerances = false
  EqualTolerance = true
  FormatSpec = ⌀%.2f
  FormatSpecOverTolerance = %+.2f
  FormatSpecUnderTolerance = %+.2f
  Inverted = false
  LockPosition = false
  MeasureType = 1
  OverTolerance = 0
  References2D = -> [View005]
  Rotation = 0
  ScaleType = 0
  TheoreticalExact = false
  Type = 5
  UnderTolerance = 0
  X = -76.3769
  Y = 4.56435
FEATURE [TechDraw::DrawViewDimension] Dimension040
  Arbitrary = false
  ArbitraryTolerances = false
  EqualTolerance = true
  FormatSpec = %.2f
  FormatSpecOverTolerance = %+.2f
  FormatSpecUnderTolerance = %+.2f
  Inverted = false
  LockPosition = false
  MeasureType = 1
  OverTolerance = 0
  References2D = -> [View005]
  Rotation = 0
  ScaleType = 0
  TheoreticalExact = false
  Type = 2
  UnderTolerance = 0
  X = 12.5774
  Y = 24.4401
FEATURE [TechDraw::DrawPage] Page005  label="BaseHolder_Cotas"
  KeepUpdated = true
  NextBalloonIndex = 1
  ProjectionType = 0
  Template = -> Template005
  Views = -> [View005,Dimension029,Dimension030,Dimension031,Dimension032,Dimension033,Dimension034,Dimension035,Dimension036,Dimension037,Dimension038,Dimension039,Dimension040]
FEATURE [TechDraw::DrawSVGTemplate] Template006
  EditableTexts = Designed_by_Name=<owner>; Drawing_number=001; FC-Date=15/8/21; FC-SC=1:1; FC-SH=3/8; FC-Title=DrillHolder_Section; Subtitle=Soporte Taladro; Weight=<250gr
  Height = 210
  Orientation = 1
  Width = 297
FEATURE [TechDraw::DrawViewPart] View006
  CoarseView = false
  Direction = (0,1,0)
  Focus = 100
  HardHidden = false
  IsoCount = 0
  IsoHidden = false
  IsoVisible = false
  LockPosition = false
  Perspective = false
  Rotation = 0
  ScaleType = 0
  SeamHidden = false
  SeamVisible = true
  SmoothHidden = false
  SmoothVisible = true
  Source = -> [Chamfer007]
  X = 80.4686
  XDirection = (-1,0,0)
  Y = 133.924
FEATURE [TechDraw::DrawViewSection] SectionView  label="Section  - "
  BaseView = -> View006
  CoarseView = false
  CutSurfaceDisplay = 2
  Direction = (1,0,0)
  FileGeomPattern = /snap/freecad/22/opt/local/FreeCAD-0.19/share/Mod/TechDraw/PAT/FCPAT.pat
  FileHatchPattern = /snap/freecad/22/opt/local/FreeCAD-0.19/share/Mod/TechDraw/Patterns/simple.svg
  Focus = 100
  FuseBeforeCut = false
  HardHidden = false
  HatchScale = 1
  IsoCount = 0
  IsoHidden = false
  IsoVisible = false
  LockPosition = false
  NameGeomPattern = Diamond
  Perspective = false
  Rotation = 0
  ScaleType = 0
  SeamHidden = false
  SeamVisible = true
  SectionDirection = 0
  SectionNormal = (1,0,0)
  SectionOrigin = (15.9,365.11,-146.25)
  SmoothHidden = false
  SmoothVisible = true
  Source = -> [Chamfer007]
  X = 191.357
  XDirection = (0,1,0)
  Y = 134.61
FEATURE [TechDraw::DrawViewDimension] Dimension041
  Arbitrary = false
  ArbitraryTolerances = false
  EqualTolerance = true
  FormatSpec = %.2f
  FormatSpecOverTolerance = %+.2f
  FormatSpecUnderTolerance = %+.2f
  Inverted = false
  LockPosition = false
  MeasureType = 1
  OverTolerance = 0
  References2D = -> [SectionView]
  Rotation = 0
  ScaleType = 0
  TheoreticalExact = false
  Type = 6
  UnderTolerance = 0
  X = 47.7103
  Y = -0.617472
FEATURE [TechDraw::DrawViewDimension] Dimension042
  Arbitrary = false
  ArbitraryTolerances = false
  EqualTolerance = true
  FormatSpec = %.2f
  FormatSpecOverTolerance = %+.2f
  FormatSpecUnderTolerance = %+.2f
  Inverted = false
  LockPosition = false
  MeasureType = 1
  OverTolerance = 0
  References2D = -> [SectionView]
  Rotation = 0
  ScaleType = 0
  TheoreticalExact = false
  Type = 0
  UnderTolerance = 0
  X = -43.959
  Y = 4.41746
FEATURE [TechDraw::DrawViewDimension] Dimension043
  Arbitrary = false
  ArbitraryTolerances = false
  EqualTolerance = true
  FormatSpec = %.2f
  FormatSpecOverTolerance = %+.2f
  FormatSpecUnderTolerance = %+.2f
  Inverted = false
  LockPosition = false
  MeasureType = 1
  OverTolerance = 0
  References2D = -> [SectionView]
  Rotation = 0
  ScaleType = 0
  TheoreticalExact = false
  Type = 0
  UnderTolerance = 0
  X = -2.85713
  Y = 5.70759
FEATURE [TechDraw::DrawViewDimension] Dimension044
  Arbitrary = false
  ArbitraryTolerances = false
  EqualTolerance = true
  FormatSpec = %.2f
  FormatSpecOverTolerance = %+.2f
  FormatSpecUnderTolerance = %+.2f
  Inverted = false
  LockPosition = false
  MeasureType = 1
  OverTolerance = 0
  References2D = -> [View006]
  Rotation = 0
  ScaleType = 0
  TheoreticalExact = false
  Type = 1
  UnderTolerance = 0
  X = -5.78376
  Y = -4.13837
FEATURE [TechDraw::DrawViewDimension] Dimension045
  Arbitrary = false
  ArbitraryTolerances = false
  EqualTolerance = true
  FormatSpec = %.2f
  FormatSpecOverTolerance = %+.2f
  FormatSpecUnderTolerance = %+.2f
  Inverted = false
  LockPosition = false
  MeasureType = 1
  OverTolerance = 0
  References2D = -> [View006]
  Rotation = 0
  ScaleType = 0
  TheoreticalExact = false
  Type = 1
  UnderTolerance = 0
  X = 0.476322
  Y = 45.0877
FEATURE [TechDraw::DrawViewDimension] Dimension046
  Arbitrary = false
  ArbitraryTolerances = false
  EqualTolerance = true
  FormatSpec = %.2f
  FormatSpecOverTolerance = %+.2f
  FormatSpecUnderTolerance = %+.2f
  Inverted = false
  LockPosition = false
  MeasureType = 1
  OverTolerance = 0
  References2D = -> [View006]
  Rotation = 0
  ScaleType = 0
  TheoreticalExact = false
  Type = 2
  UnderTolerance = 0
  X = 27.0346
  Y = 17.3743
FEATURE [TechDraw::DrawViewDimension] Dimension047
  Arbitrary = false
  ArbitraryTolerances = false
  EqualTolerance = true
  FormatSpec = %.2f
  FormatSpecOverTolerance = %+.2f
  FormatSpecUnderTolerance = %+.2f
  Inverted = false
  LockPosition = false
  MeasureType = 1
  OverTolerance = 0
  References2D = -> [View006]
  Rotation = 0
  ScaleType = 0
  TheoreticalExact = false
  Type = 0
  UnderTolerance = 0
  X = 38.5402
  Y = 45.5863
FEATURE [TechDraw::DrawPage] Page006  label="DrillHolder_Section"
  KeepUpdated = true
  NextBalloonIndex = 1
  ProjectionType = 0
  Template = -> Template006
  Views = -> [View006,SectionView,Dimension041,Dimension042,Dimension043,Dimension044,Dimension045,Dimension046,Dimension047]
FEATURE [TechDraw::DrawSVGTemplate] Template007
  EditableTexts = Designed_by_Name=<owner>; Drawing_number=001; FC-Date=15/8/21; FC-SC=1:1; FC-SH=8/8; FC-Title=ClaptonJig_Section; Subtitle=Soporte Quitavueltas; Weight=<250gr
  Height = 210
  Orientation = 1
  Width = 297
FEATURE [TechDraw::DrawViewPart] View007
  CoarseView = false
  Direction = (0,1,0)
  Focus = 100
  HardHidden = false
  IsoCount = 0
  IsoHidden = false
  IsoVisible = false
  LockPosition = false
  Perspective = false
  Rotation = 0
  ScaleType = 0
  SeamHidden = false
  SeamVisible = true
  SmoothHidden = false
  SmoothVisible = true
  Source = -> [Part__Feature003]
  X = 71.3571
  XDirection = (-1,0,0)
  Y = 152.143
FEATURE [TechDraw::DrawViewSection] SectionView001  label="Section  - 001"
  BaseView = -> View007
  CoarseView = false
  CutSurfaceDisplay = 2
  Direction = (1,0,0)
  FileGeomPattern = /snap/freecad/22/opt/local/FreeCAD-0.19/share/Mod/TechDraw/PAT/FCPAT.pat
  FileHatchPattern = /snap/freecad/22/opt/local/FreeCAD-0.19/share/Mod/TechDraw/Patterns/simple.svg
  Focus = 100
  FuseBeforeCut = false
  HardHidden = false
  HatchScale = 1
  IsoCount = 0
  IsoHidden = false
  IsoVisible = false
  LockPosition = false
  NameGeomPattern = Diamond
  Perspective = false
  Rotation = 0
  ScaleType = 0
  SeamHidden = false
  SeamVisible = true
  SectionDirection = 0
  SectionNormal = (1,0,0)
  SectionOrigin = (15.95,32.61,2.69)
  SmoothHidden = false
  SmoothVisible = true
  Source = -> [Part__Feature003]
  X = 197.201
  XDirection = (0,1,0)
  Y = 154.87
FEATURE [TechDraw::DrawViewDimension] Dimension048
  Arbitrary = false
  ArbitraryTolerances = false
  EqualTolerance = true
  FormatSpec = %.2f
  FormatSpecOverTolerance = %+.2f
  FormatSpecUnderTolerance = %+.2f
  Inverted = false
  LockPosition = false
  MeasureType = 1
  OverTolerance = 0
  References2D = -> [SectionView001]
  Rotation = 0
  ScaleType = 0
  TheoreticalExact = false
  Type = 2
  UnderTolerance = 0
  X = 38.8122
  Y = 0
FEATURE [TechDraw::DrawViewDimension] Dimension049
  Arbitrary = false
  ArbitraryTolerances = false
  EqualTolerance = true
  FormatSpec = %.2f
  FormatSpecOverTolerance = %+.2f
  FormatSpecUnderTolerance = %+.2f
  Inverted = false
  LockPosition = false
  MeasureType = 1
  OverTolerance = 0
  References2D = -> [SectionView001]
  Rotation = 0
  ScaleType = 0
  TheoreticalExact = false
  Type = 2
  UnderTolerance = 0
  X = 19.6807
  Y = -18.4896
FEATURE [TechDraw::DrawViewDimension] Dimension050
  Arbitrary = false
  ArbitraryTolerances = false
  EqualTolerance = true
  FormatSpec = %.2f
  FormatSpecOverTolerance = %+.2f
  FormatSpecUnderTolerance = %+.2f
  Inverted = false
  LockPosition = false
  MeasureType = 1
  OverTolerance = 0
  References2D = -> [SectionView001]
  Rotation = 0
  ScaleType = 0
  TheoreticalExact = false
  Type = 1
  UnderTolerance = 0
  X = -48.1216
  Y = -37.2368
FEATURE [TechDraw::DrawViewDimension] Dimension051
  Arbitrary = false
  ArbitraryTolerances = false
  EqualTolerance = true
  FormatSpec = %.2f
  FormatSpecOverTolerance = %+.2f
  FormatSpecUnderTolerance = %+.2f
  Inverted = false
  LockPosition = false
  MeasureType = 1
  OverTolerance = 0
  References2D = -> [SectionView001]
  Rotation = 0
  ScaleType = 0
  TheoreticalExact = false
  Type = 2
  UnderTolerance = 0
  X = -50.081
  Y = 1.55965
FEATURE [TechDraw::DrawViewDimension] Dimension052
  Arbitrary = false
  ArbitraryTolerances = false
  EqualTolerance = true
  FormatSpec = %.2f
  FormatSpecOverTolerance = %+.2f
  FormatSpecUnderTolerance = %+.2f
  Inverted = false
  LockPosition = false
  MeasureType = 1
  OverTolerance = 0
  References2D = -> [SectionView001]
  Rotation = 0
  ScaleType = 0
  TheoreticalExact = false
  Type = 1
  UnderTolerance = 0
  X = -15.1412
  Y = 22.5901
FEATURE [TechDraw::DrawViewDimension] Dimension053
  Arbitrary = false
  ArbitraryTolerances = false
  EqualTolerance = true
  FormatSpec = %.2f
  FormatSpecOverTolerance = %+.2f
  FormatSpecUnderTolerance = %+.2f
  Inverted = false
  LockPosition = false
  MeasureType = 1
  OverTolerance = 0
  References2D = -> [SectionView001]
  Rotation = 0
  ScaleType = 0
  TheoreticalExact = false
  Type = 1
  UnderTolerance = 0
  X = -3.13672
  Y = 40.849
FEATURE [TechDraw::DrawViewDimension] Dimension054
  Arbitrary = false
  ArbitraryTolerances = false
  EqualTolerance = true
  FormatSpec = %.2f
  FormatSpecOverTolerance = %+.2f
  FormatSpecUnderTolerance = %+.2f
  Inverted = false
  LockPosition = false
  MeasureType = 1
  OverTolerance = 0
  References2D = -> [View007]
  Rotation = 0
  ScaleType = 0
  TheoreticalExact = false
  Type = 1
  UnderTolerance = 0
  X = -5.47053
  Y = -11.3242
FEATURE [TechDraw::DrawViewDimension] Dimension055
  Arbitrary = false
  ArbitraryTolerances = false
  EqualTolerance = true
  FormatSpec = %.2f
  FormatSpecOverTolerance = %+.2f
  FormatSpecUnderTolerance = %+.2f
  Inverted = false
  LockPosition = false
  MeasureType = 1
  OverTolerance = 0
  References2D = -> [View007]
  Rotation = 0
  ScaleType = 0
  TheoreticalExact = false
  Type = 1
  UnderTolerance = 0
  X = 1.28101
  Y = -21.3367
FEATURE [TechDraw::DrawViewDimension] Dimension056
  Arbitrary = false
  ArbitraryTolerances = false
  EqualTolerance = true
  FormatSpec = %.2f
  FormatSpecOverTolerance = %+.2f
  FormatSpecUnderTolerance = %+.2f
  Inverted = false
  LockPosition = false
  MeasureType = 1
  OverTolerance = 0
  References2D = -> [View007]
  Rotation = 0
  ScaleType = 0
  TheoreticalExact = false
  Type = 2
  UnderTolerance = 0
  X = -27.9006
  Y = 0.559917
FEATURE [TechDraw::DrawPage] Page007  label="ClaptonJig_Section"
  KeepUpdated = true
  NextBalloonIndex = 1
  ProjectionType = 0
  Template = -> Template007
  Views = -> [View007,SectionView001,Dimension048,Dimension049,Dimension050,Dimension051,Dimension052,Dimension053,Dimension054,Dimension055,Dimension056]
